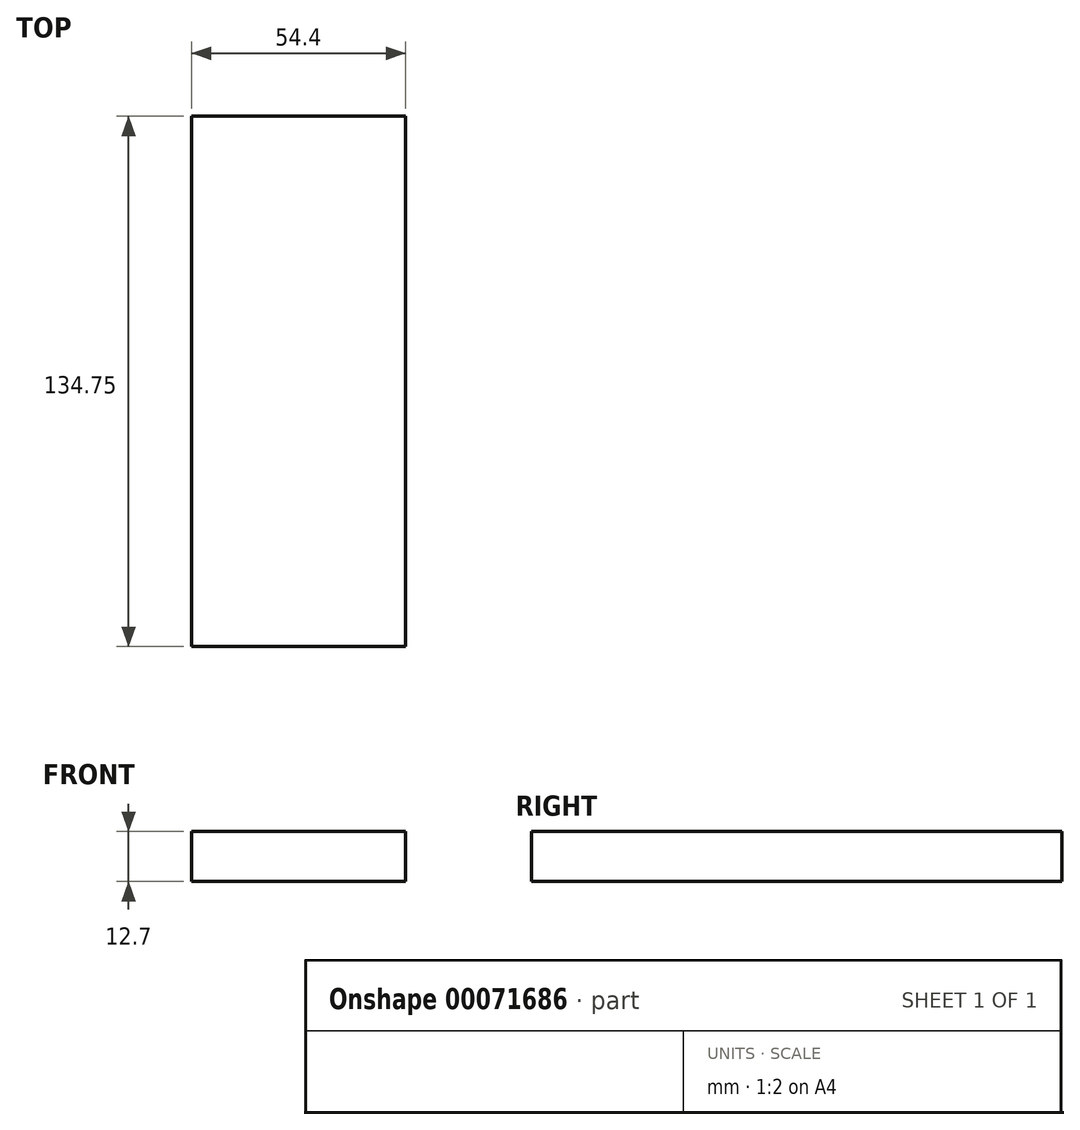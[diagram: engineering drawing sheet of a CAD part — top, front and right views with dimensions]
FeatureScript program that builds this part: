
annotation { "Feature Type Name" : "Feature", "Feature Type Description" : "" }
export const myFeature = defineFeature(function(context is Context, id is Id, definition is map)
    precondition{}
    {
        {
            var Q0;
            Q0=qCreatedBy(makeId("Top.planeOp"),FACE);
            var sketch = newSketch(context, id + "F0", { "sketchPlane" : qUnion([Q0])});
            skLineSegment(sketch, "E0.bottom", {"start": v(-68.27, 64.72) * mm, "end": v(-13.87, 64.72) * mm});
            skLineSegment(sketch, "E0.top", {"start": v(-68.27, -70.03) * mm, "end": v(-13.87, -70.03) * mm});
            skLineSegment(sketch, "E0.left", {"start": v(-68.27, 64.72) * mm, "end": v(-68.27, -70.03) * mm});
            skLineSegment(sketch, "E0.right", {"start": v(-13.87, 64.72) * mm, "end": v(-13.87, -70.03) * mm});
            skSolve(sketch);
        }
        {
            var Q0;
            Q0 = qSketchRegion(id + "F0", true);
            extrude(context, id + "F1", {"entities" : qUnion([Q0]), "depth" : 12.7 * mm});
        }
    });
